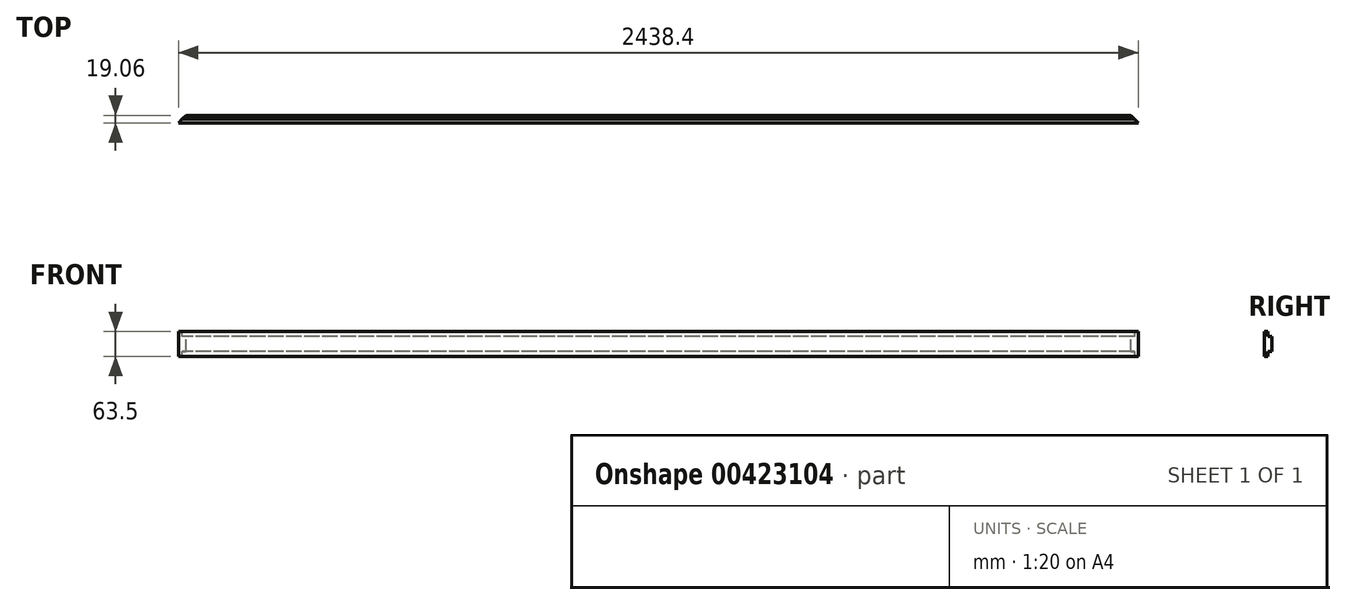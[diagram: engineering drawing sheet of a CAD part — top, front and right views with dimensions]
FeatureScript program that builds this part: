
annotation { "Feature Type Name" : "Feature", "Feature Type Description" : "" }
export const myFeature = defineFeature(function(context is Context, id is Id, definition is map)
    precondition{}
    {
        {
            var Q0;
            Q0=qCreatedBy(makeId("Right.planeOp"),FACE);
            var sketch = newSketch(context, id + "F0", { "sketchPlane" : qUnion([Q0])});
            skLineSegment(sketch, "E0.bottom", {"start": v(-9.53, 31.75) * mm, "end": v(0, 31.75) * mm});
            skLineSegment(sketch, "E0.top", {"start": v(-9.52, -31.75) * mm, "end": v(0, -31.75) * mm});
            skLineSegment(sketch, "E0.left", {"start": v(-9.53, 31.75) * mm, "end": v(-9.52, -31.75) * mm});
            skLineSegment(sketch, "E0.right", {"start": v(9.52, 19.05) * mm, "end": v(9.53, -19.05) * mm});
            skPoint(sketch, "E0.middle", {"position": v(0, 0) * mm});
            skLineSegment(sketch, "E1", {"start": v(0, 31.75) * mm, "end": v(0, 19.05) * mm});
            skPoint(sketch, "E1.endSnap0", {"position": v(0, 31.75) * mm});
            skLineSegment(sketch, "E2", {"start": v(0, 19.05) * mm, "end": v(9.52, 19.05) * mm});
            skLineSegment(sketch, "E3", {"start": v(9.52, -19.05) * mm, "end": v(0, -19.05) * mm});
            skLineSegment(sketch, "E4", {"start": v(0, -19.05) * mm, "end": v(0, -31.75) * mm});
            skSolve(sketch);
        }
        {
            var Q0;
            Q0=makeQuery(id+"F0.imprint","IMPRINT",FACE,{"disambiguationData":[TD([[makeQuery(id+"F0.imprint","IMPRINT",EDGE,{"derivedFrom":sQuery(id+"F0.wireOp",EDGE,"E0.bottom")}),-1.0]])]});
            extrude(context, id + "F1", {"entities" : qUnion([Q0]), "depth" : 1219.2 * mm, "hasSecondDirection" : true, "secondDirectionOppositeDirection" : true, "secondDirectionDepth" : 1219.2 * mm});
        }
        {
            var Q0;
            Q0=makeQuery(id+"F1.opExtrude","SWEPT_FACE",FACE,{"disambiguationData":[OSD([sQuery(id+"F0.wireOp",EDGE,"E0.bottom")])]});
            var sketch = newSketch(context, id + "F2", { "sketchPlane" : qUnion([Q0])});
            skLineSegment(sketch, "E5", {"start": v(1219.2, -9.53) * mm, "end": v(1200.15, 9.52) * mm});
            skLineSegment(sketch, "E6", {"start": v(1219.2, -9.53) * mm, "end": v(1219.2, 9.53) * mm});
            skLineSegment(sketch, "E7", {"start": v(1219.2, 9.53) * mm, "end": v(1200.15, 9.52) * mm});
            skLineSegment(sketch, "E8", {"start": v(-1219.2, -9.53) * mm, "end": v(-1219.2, 9.52) * mm});
            skLineSegment(sketch, "E9", {"start": v(-1219.2, 9.52) * mm, "end": v(-1200.15, 9.52) * mm});
            skLineSegment(sketch, "E10", {"start": v(-1200.15, 9.53) * mm, "end": v(-1219.2, -9.52) * mm});
            skSolve(sketch);
        }
        {
            var Q0;
            {var subQ3=sQuery(id+"F2.wireOp",EDGE,"E9");Q0=makeQuery(id+"F2.imprint","IMPRINT",FACE,{"disambiguationData":[TD([[makeQuery(id+"F2.imprint","IMPRINT",EDGE,{"derivedFrom":subQ3}),-1.0]])]});}
            var Q1;
            {var subQ1=sQuery(id+"F2.wireOp",EDGE,"E8");var subQ2=sQuery(id+"F0.wireOp",EDGE,"E0.bottom");var subQ4=makeQuery(id+"F1.opExtrude","SWEPT_EDGE",EDGE,{"disambiguationData":[OSD([subQ2,sQuery(id+"F0.wireOp",EDGE,"E1")])]});var subQ5=makeQuery(id+"F2.imprint","INTERSECT",VERTEX,{"derivedFrom":[subQ4,subQ1]});Q1=makeQuery(id+"F2.imprint","IMPRINT",FACE,{"disambiguationData":[TD([[makeQuery(id+"F2.imprint","IMPRINT",EDGE,{"disambiguationData":[TD([[subQ5,1.0]])],"derivedFrom":subQ1}),-1.0]])]});}
            var Q2;
            {var subQ0=sQuery(id+"F2.wireOp",EDGE,"E7");Q2=makeQuery(id+"F2.imprint","IMPRINT",FACE,{"disambiguationData":[TD([[makeQuery(id+"F2.imprint","IMPRINT",EDGE,{"derivedFrom":subQ0}),1.0]])]});}
            var Q3;
            {var subQ1=sQuery(id+"F2.wireOp",EDGE,"E5");var subQ2=sQuery(id+"F0.wireOp",EDGE,"E0.bottom");var subQ4=makeQuery(id+"F1.opExtrude","SWEPT_EDGE",EDGE,{"disambiguationData":[OSD([subQ2,sQuery(id+"F0.wireOp",EDGE,"E1")])]});var subQ5=makeQuery(id+"F2.imprint","INTERSECT",VERTEX,{"derivedFrom":[subQ4,subQ1]});Q3=makeQuery(id+"F2.imprint","IMPRINT",FACE,{"disambiguationData":[TD([[makeQuery(id+"F2.imprint","IMPRINT",EDGE,{"disambiguationData":[TD([[subQ5,1.0]])],"derivedFrom":subQ1}),-1.0]])]});}
            extrude(context, id + "F3", {"entities" : qUnion([Q0, Q1, Q2, Q3]), "operationType" : NewBodyOperationType.REMOVE, "endBound" : BoundingType.THROUGH_ALL, "oppositeDirection" : true, "depth" : 25.4 * mm});
        }
    });
